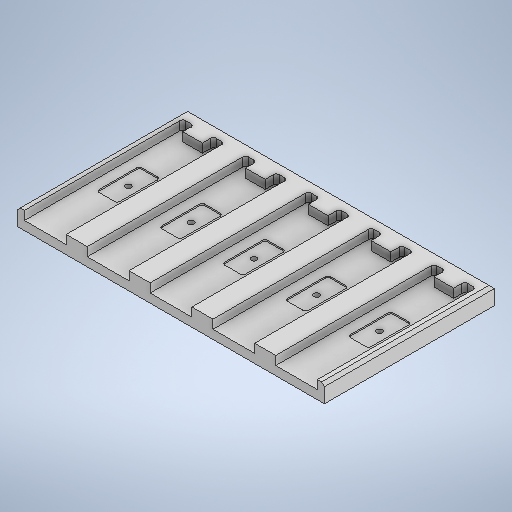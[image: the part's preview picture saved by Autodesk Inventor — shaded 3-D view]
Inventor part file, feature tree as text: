
AUTODESK INVENTOR PART (.ipt)
format: ipt  version: 2025 (Build 290162000, 162)  size: 427,008 bytes
history: native  units: mm
features: sketch x5, extrude x3, hole x1, chamfer x1
ambient origin geometry x8: Origin, YZ Plane, XZ Plane, XY Plane, X Axis, Y Axis, Z Axis, Center Point
bodies: Solid1 (feature_tree)
feature tree (10):
  extrude  "Extrusion1"  Depth=123.0mm
  extrude  "Extrusion2"  Depth=30.2mm
  sketch  "Sketch3"  dims[d9=8.0mm d10=2.0mm d11=50.0mm d13=45.45mm d14=10.0mm d16=10.0mm d18=6.35mm d19=0.0mm d20=31.0mm d21=15.0mm d22=31.0mm d23=30.2mm d24=7.6mm d25=2.0mm d26=15.5mm d27=7.5mm d28=50.0mm d30=45.45mm d31=10.0mm d33=10.0mm d35=1.0mm d36=0.0mm d37=4.0mm d38=6.0mm d39=11.113mm d40=6.35mm d41=14.3117mm d42=8.0mm d43=20.594885mm d44=2.0mm d45=2.0mm d46=45.0deg]
  extrude  "Extrusion3"  Depth=5.0mm
  hole  "Hole1"  [1 undecoded]
  chamfer  "Chamfer1"  Distance=2.0mm
  sketch  "Sketch1"  dims[d0=222.0mm d1=123.0mm]
  sketch  "Sketch2"  dims[d5=45.0mm d6=5.0mm]
  sketch  "Sketch Rectangular Pattern1"  dims[d2=12.7mm d3=0.0mm d4=30.2mm]
  sketch  "Sketch Rectangular Pattern2"  dims[d7=8.0mm d8=8.0mm]
note: 1 required parameter value undecoded (feature->parameter linkage not recoverable at this tier; creation-order binding heuristic only, values carry confidence <= 0.55)
